annotation { "Feature Type Name" : "Feature", "Feature Type Description" : "" }
export const myFeature = defineFeature(function(context is Context, id is Id, definition is map)
    precondition{}
    {
        {
            var Q0;
            Q0=qCreatedBy(makeId("Front.planeOp"),FACE);
            var sketch = newSketch(context, id + "F0", { "sketchPlane" : qUnion([Q0])});
            skArc(sketch, "E0", {"start": v(44.45, 0) * mm, "mid": v(-0.13, 44.7) * mm, "end": v(-44.7, 0) * mm});
            skArc(sketch, "E1.0", {"start": v(50.8, -0.02) * mm, "mid": v(44.75, 24.18) * mm, "end": v(27.94, 42.61) * mm});
            skLineSegment(sketch, "E2", {"start": v(-51.06, -0.02) * mm, "end": v(-44.7, 0) * mm});
            skLineSegment(sketch, "E3", {"start": v(44.45, 0) * mm, "end": v(50.8, -0.02) * mm});
            skLineSegment(sketch, "E4", {"start": v(-21.6, 62.93) * mm, "end": v(21.59, 62.93) * mm});
            skLineSegment(sketch, "E5", {"start": v(-21.6, 62.93) * mm, "end": v(-27.94, 62.93) * mm});
            skLineSegment(sketch, "E6", {"start": v(-27.94, 62.93) * mm, "end": v(-27.94, 42.78) * mm});
            skLineSegment(sketch, "E7", {"start": v(21.59, 62.93) * mm, "end": v(27.94, 62.93) * mm});
            skLineSegment(sketch, "E8", {"start": v(27.94, 62.93) * mm, "end": v(27.94, 42.61) * mm});
            skArc(sketch, "E9.trimOffspring", {"start": v(-27.94, 42.78) * mm, "mid": v(-44.94, 24.32) * mm, "end": v(-51.06, -0.02) * mm});
            skSolve(sketch);
        }
        {
            var Q0;
            Q0=makeQuery(id+"F0.imprint","IMPRINT",FACE,{"disambiguationData":[TD([[makeQuery(id+"F0.imprint","IMPRINT",EDGE,{"derivedFrom":sQuery(id+"F0.wireOp",EDGE,"E0")}),-1.0]])]});
            extrude(context, id + "F1", {"entities" : qUnion([Q0]), "oppositeDirection" : true, "depth" : 254 * mm});
        }
        {
            var Q0;
            Q0=makeQuery(id+"F1.opExtrude","SWEPT_FACE",FACE,{"disambiguationData":[OSD([sQuery(id+"F0.wireOp",EDGE,"E4"),sQuery(id+"F0.wireOp",EDGE,"E5"),sQuery(id+"F0.wireOp",EDGE,"E7")])]});
            var sketch = newSketch(context, id + "F2", { "sketchPlane" : qUnion([Q0])});
            skLineSegment(sketch, "E10.0", {"start": v(-21.6, 247.65) * mm, "end": v(-21.6, 6.35) * mm});
            skLineSegment(sketch, "E10.1", {"start": v(-21.6, 247.65) * mm, "end": v(21.59, 247.65) * mm});
            skLineSegment(sketch, "E10.2", {"start": v(21.59, 247.65) * mm, "end": v(21.59, 6.35) * mm});
            skLineSegment(sketch, "E10.3", {"start": v(-21.6, 6.35) * mm, "end": v(21.59, 6.35) * mm});
            skSolve(sketch);
        }
        {
            var Q0;
            Q0=makeQuery(id+"F2.imprint","IMPRINT",FACE,{"disambiguationData":[TD([[makeQuery(id+"F2.imprint","IMPRINT",EDGE,{"derivedFrom":sQuery(id+"F2.wireOp",EDGE,"E10.0")}),1.0]])]});
            extrude(context, id + "F3", {"entities" : qUnion([Q0]), "operationType" : NewBodyOperationType.REMOVE, "oppositeDirection" : true, "depth" : 25.4 * mm});
        }
        {
            var Q0;
            Q0=makeQuery(id+"F1.opExtrude","SWEPT_FACE",FACE,{"disambiguationData":[OSD([sQuery(id+"F0.wireOp",EDGE,"E8")])]});
            var sketch = newSketch(context, id + "F4", { "sketchPlane" : qUnion([Q0])});
            skText(sketch, "E11", { "text": "Certified Technologies", "fontName": "OpenSans-Regular.ttf"});
            skLineSegment(sketch, "E12", {"start": v(127, 62.93) * mm, "end": v(127, 59.85) * mm, "construction": true});
            const initialGuessF4  = {"E11": [0.03412, 0.04695, 1, 0, 0.0129]};
            skSetInitialGuess(sketch, initialGuessF4);
            skSolve(sketch);
        }
        {
            var Q0;
            Q0 = qSketchRegion(id + "F4", true);
            extrude(context, id + "F5", {"entities" : qUnion([Q0]), "operationType" : NewBodyOperationType.REMOVE, "oppositeDirection" : true, "depth" : 2.54 * mm});
        }
        {
            var Q0;
            Q0=makeQuery(id+"F3.boolean.opBoolean","COPY",FACE,{"derivedFrom":makeQuery(id+"F3.opExtrude","SWEPT_FACE",FACE,{"disambiguationData":[OSD([sQuery(id+"F2.wireOp",EDGE,"E10.0")])]})});
            var sketch = newSketch(context, id + "F6", { "sketchPlane" : qUnion([Q0])});
            skText(sketch, "E13", { "text": "Isaac", "fontName": "OpenSans-Regular.ttf"});
            const initialGuessF6  = {"E13": [0.2339, 0.0405, 1, 0, 0.00381]};
            skSetInitialGuess(sketch, initialGuessF6);
            skSolve(sketch);
        }
        {
            var Q0;
            Q0 = qSketchRegion(id + "F6", true);
            extrude(context, id + "F7", {"entities" : qUnion([Q0]), "operationType" : NewBodyOperationType.REMOVE, "oppositeDirection" : true, "depth" : 2.54 * mm});
        }
    });